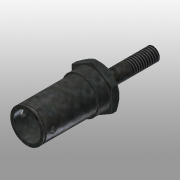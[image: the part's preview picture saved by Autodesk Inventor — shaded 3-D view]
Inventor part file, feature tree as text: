
AUTODESK INVENTOR PART (.ipt)
format: ipt  version: 2015 (Build 190159000, 159)  size: 156,672 bytes
history: native  units: mm
features: sketch x8, other x3
ambient origin geometry x8: Origin, YZ Plane, XZ Plane, XY Plane, X Axis, Y Axis, Z Axis, Center Point
bodies: Solid1 (feature_tree)
feature tree (11):
  other  "500-126.ipt"
  other  "Solid1::500-126.ipt"
  other  "TaggingFeature1"
  sketch  "Sketch1"  dims[d0=10.0mm]
  sketch  "Sketch2"
  sketch  "Sketch3"
  sketch  "Sketch4"
  sketch  "Sketch5"
  sketch  "Sketch6"
  sketch  "Sketch7"
  sketch  "Sketch8"
